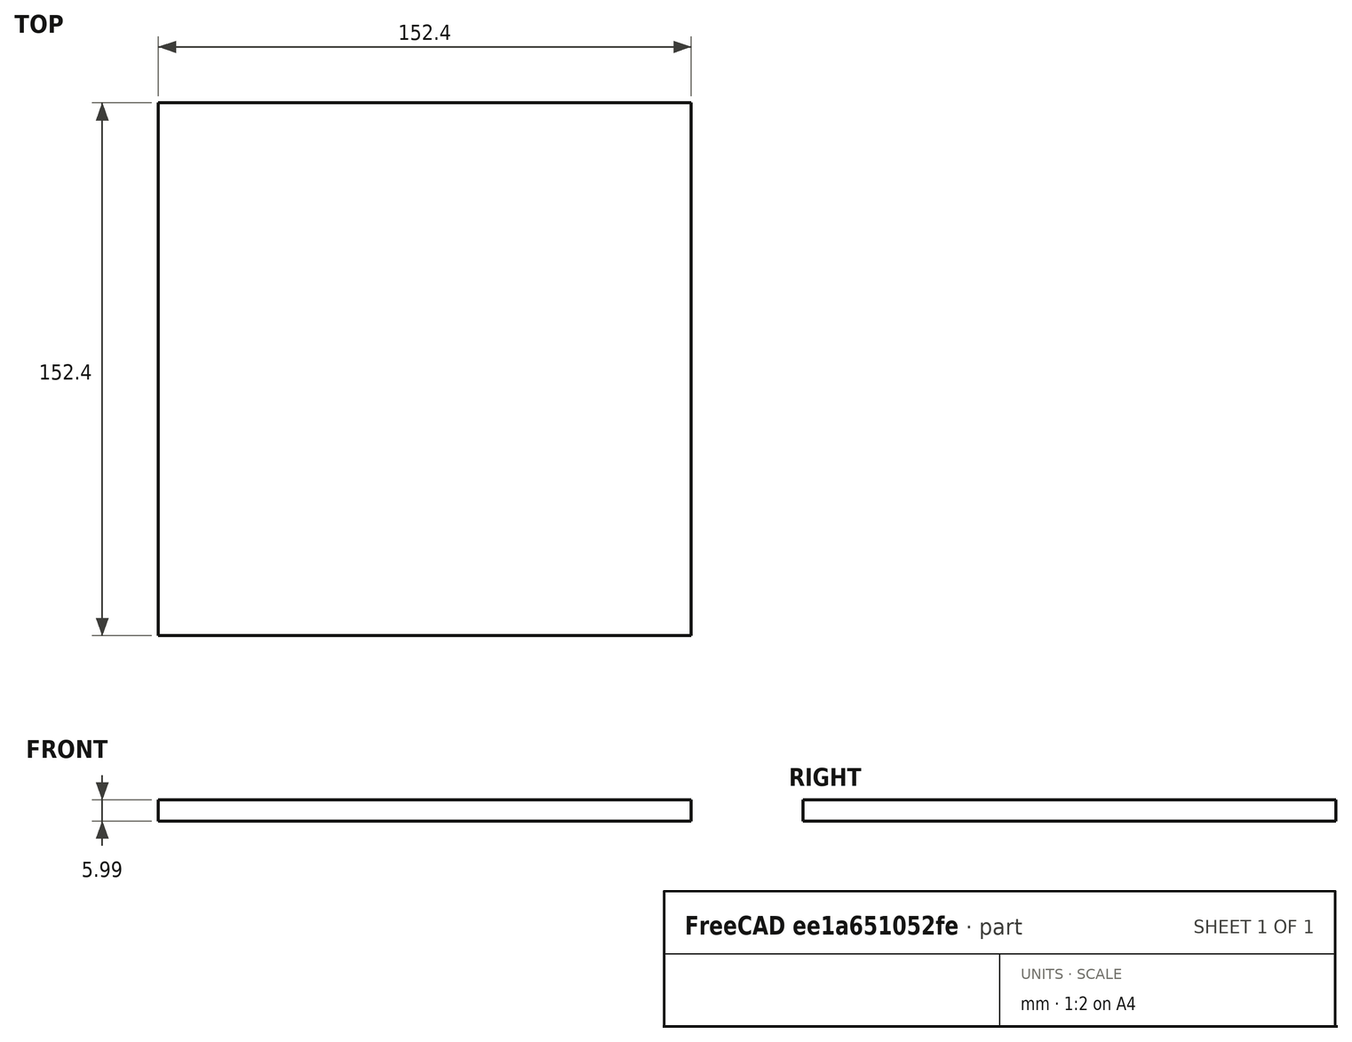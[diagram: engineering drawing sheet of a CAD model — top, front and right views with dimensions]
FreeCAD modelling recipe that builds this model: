
FCSTD DOCUMENT  (FreeCAD 0.19R24267 (Git))
Label: Inv2-P5
License: All rights reserved
LicenseURL: http://en.wikipedia.org/wiki/All_rights_reserved
objects: TechDraw::DrawViewDimension×3, TechDraw::DrawProjGroupItem×2, TechDraw::DrawHatch×2, TechDraw::DrawViewAnnotation×2, Sketcher::SketchObject×1, Part::Extrusion×1, TechDraw::DrawSVGTemplate×1, TechDraw::DrawProjGroup×1, TechDraw::DrawPage×1
note: 2 computed .brp shape members not serialized (recipe doc carries the construction recipe); baked Part::Feature solids carry a one-line shape summary decoded from their .brp

FEATURE [Sketcher::SketchObject] Sketch
  FullyConstrained = false
  sketch-geometry (4):
    g0: LineSegment StartX=-84.2577 StartY=77.5623 StartZ=0 EndX=68.1423 EndY=77.5623 EndZ=0
    g1: LineSegment StartX=68.1423 StartY=77.5623 StartZ=0 EndX=68.1423 EndY=-74.8377 EndZ=0
    g2: LineSegment StartX=68.1423 StartY=-74.8377 StartZ=0 EndX=-84.2577 EndY=-74.8377 EndZ=0
    g3: LineSegment StartX=-84.2577 StartY=-74.8377 StartZ=0 EndX=-84.2577 EndY=77.5623 EndZ=0
  constraints (10):
    c: Coincident(g0,g1)
    c: Coincident(g1,g2)
    c: Coincident(g2,g3)
    c: Coincident(g3,g0)
    c: Horizontal(g0)
    c: Horizontal(g2)
    c: Vertical(g1)
    c: Vertical(g3)
    c: DistanceX(g0,g0) = 152.4
    c: DistanceY(g3,g3) = 152.4
FEATURE [Part::Extrusion] Extrude
  Base = -> Sketch
  Dir = (0,0,1)
  DirMode = 2
  FaceMakerClass = Part::FaceMakerBullseye
  LengthFwd = 5.9944
  LengthRev = 0
  Solid = true
  Symmetric = false
FEATURE [TechDraw::DrawSVGTemplate] Template
  Height = 215.9
  Orientation = 1
  Width = 279.4
FEATURE [TechDraw::DrawProjGroupItem] ProjItem  label="Front"
  CoarseView = false
  Direction = (0,0,1)
  Focus = 100
  HardHidden = false
  IsoCount = 0
  IsoHidden = false
  IsoVisible = false
  LockPosition = true
  Perspective = false
  Rotation = 0
  RotationVector = (1,0,0)
  Scale = 0.5
  ScaleType = 2
  SeamHidden = false
  SeamVisible = true
  SmoothHidden = false
  SmoothVisible = true
  Source = -> [Extrude]
  Type = 0
  X = 0
  XDirection = (1,0,0)
  Y = 0
FEATURE [TechDraw::DrawProjGroupItem] ProjItem001  label="Left"
  CoarseView = false
  Direction = (-1,0,1e-16)
  Focus = 100
  HardHidden = false
  IsoCount = 0
  IsoHidden = false
  IsoVisible = false
  LockPosition = false
  Perspective = false
  Rotation = 0
  RotationVector = (1,0,0)
  ScaleType = 2
  SeamHidden = false
  SeamVisible = true
  SmoothHidden = false
  SmoothVisible = true
  Source = -> [Extrude]
  Type = 1
  X = 72.5738
  XDirection = (1e-16,0,1)
  Y = 0
FEATURE [TechDraw::DrawProjGroup] ProjGroup
  Anchor = -> ProjItem
  AutoDistribute = true
  LockPosition = false
  ProjectionType = 0
  Rotation = 0
  Scale = 0.5
  ScaleType = 2
  Source = -> [Extrude]
  Views = -> [ProjItem,ProjItem001]
  X = 125.125
  Y = 111.65
  spacingX = 15.0114
  spacingY = 15.0114
FEATURE [TechDraw::DrawHatch] Hatch  label="HatchF0"
  HatchPattern = <path>
  Source = -> ProjItem [Face0]
FEATURE [TechDraw::DrawHatch] Hatch001  label="Hatch001F0"
  HatchPattern = <path>
  Source = -> ProjItem001 [Face0]
FEATURE [TechDraw::DrawViewDimension] Dimension
  Arbitrary = false
  ArbitraryTolerances = false
  EqualTolerance = true
  FormatSpec = %.3f
  FormatSpecOverTolerance = %+.3f
  FormatSpecUnderTolerance = %+.3f
  Inverted = false
  LockPosition = false
  MeasureType = 1
  OverTolerance = 0
  References2D = -> [ProjItem]
  Rotation = 0
  ScaleType = 0
  TheoreticalExact = false
  Type = 2
  UnderTolerance = 0
  X = 46.7418
  Y = 0.233562
FEATURE [TechDraw::DrawViewDimension] Dimension001
  Arbitrary = false
  ArbitraryTolerances = false
  EqualTolerance = true
  FormatSpec = %.3f
  FormatSpecOverTolerance = %+.3f
  FormatSpecUnderTolerance = %+.3f
  Inverted = false
  LockPosition = false
  MeasureType = 1
  OverTolerance = 0
  References2D = -> [ProjItem]
  Rotation = 0
  ScaleType = 0
  TheoreticalExact = false
  Type = 1
  UnderTolerance = 0
  X = -0.233562
  Y = -47.9096
FEATURE [TechDraw::DrawViewDimension] Dimension002
  Arbitrary = false
  ArbitraryTolerances = false
  EqualTolerance = true
  FormatSpec = %.3f
  FormatSpecOverTolerance = %+.3f
  FormatSpecUnderTolerance = %+.3f
  Inverted = false
  LockPosition = false
  MeasureType = 1
  OverTolerance = 0
  References2D = -> [ProjItem001]
  Rotation = 0
  ScaleType = 0
  TheoreticalExact = false
  Type = 1
  UnderTolerance = 0
  X = 20.877
  Y = 26.9952
FEATURE [TechDraw::DrawViewAnnotation] Annotation
  Font = osifont
  LineSpace = 80
  LockPosition = false
  MaxWidth = -1
  Rotation = 0
  ScaleType = 0
  Text = Figure S2 (Inverted 2) | Panel 5 [door] | Quantity: 2
  TextSize = 5.0038
  TextStyle = 0
  X = 32.4922
  Y = 195.58
FEATURE [TechDraw::DrawViewAnnotation] Annotation002
  Font = osifont
  LineSpace = 80
  LockPosition = false
  MaxWidth = -1
  Rotation = 0
  ScaleType = 0
  Text = Units: Inches
  TextSize = 5.0038
  TextStyle = 0
  X = 259.08
  Y = 5.08
FEATURE [TechDraw::DrawPage] Page
  KeepUpdated = true
  NextBalloonIndex = 1
  ProjectionType = 0
  Template = -> Template
  Views = -> [ProjGroup,Dimension,Dimension001,Dimension002,Annotation,Annotation002]
note: 2 file-system paths scrubbed to <path> (originals preserved in the JSON sidecar)
